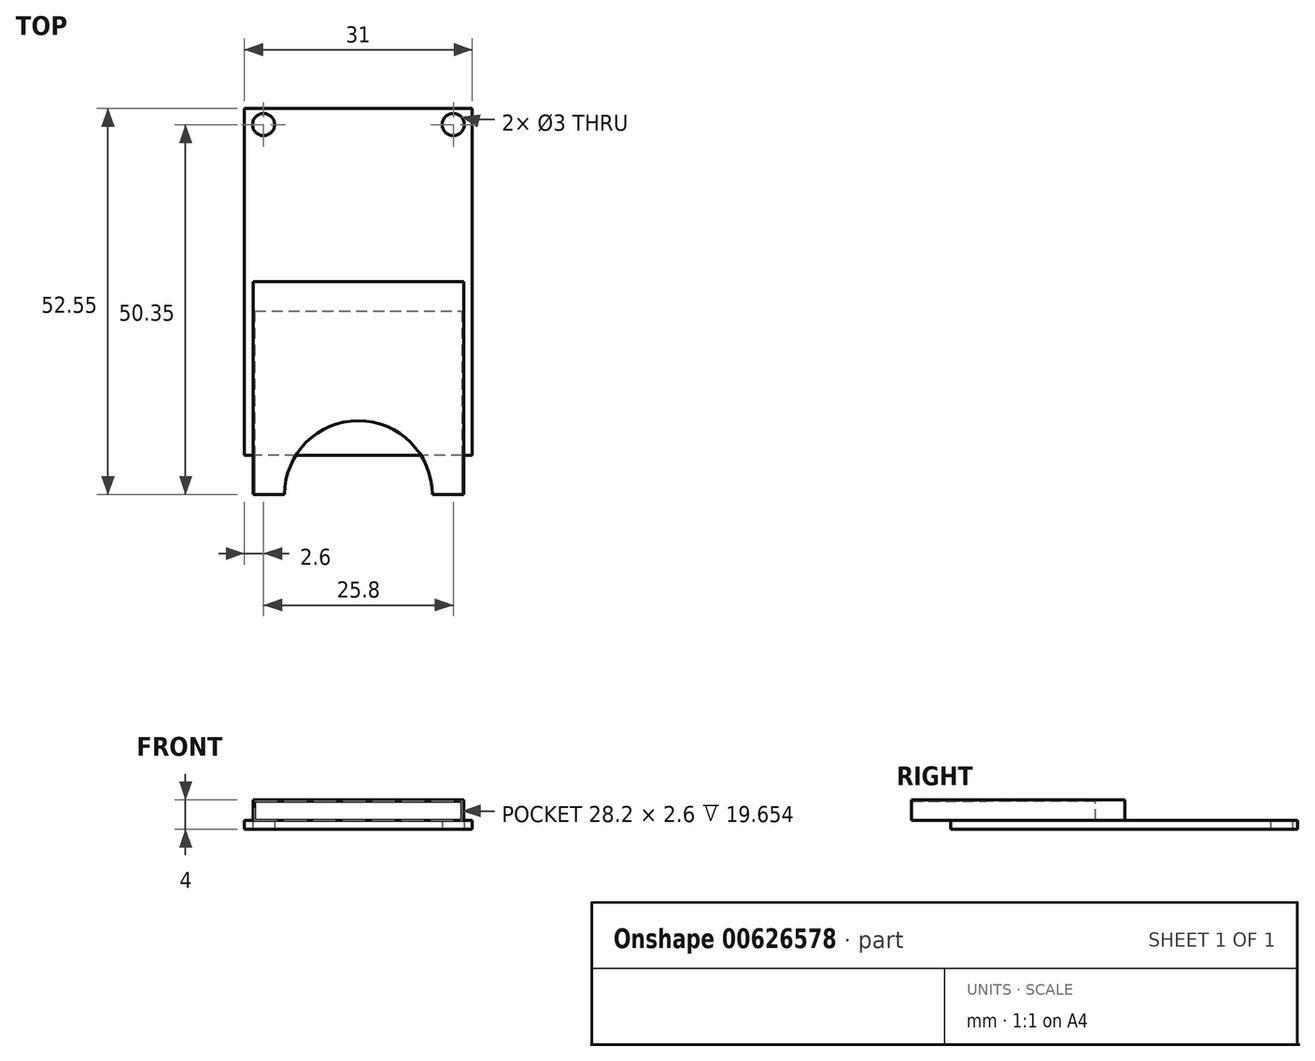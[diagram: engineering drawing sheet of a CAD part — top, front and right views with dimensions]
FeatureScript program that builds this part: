
annotation { "Feature Type Name" : "Feature", "Feature Type Description" : "" }
export const myFeature = defineFeature(function(context is Context, id is Id, definition is map)
    precondition{}
    {
        {
            var Q0;
            Q0=qCreatedBy(makeId("Top.planeOp"),FACE);
            var sketch = newSketch(context, id + "F0", { "sketchPlane" : qUnion([Q0])});
            skLineSegment(sketch, "E0.bottom", {"start": v(15.5, 23.6) * mm, "end": v(-15.5, 23.6) * mm});
            skLineSegment(sketch, "E0.top", {"start": v(15.5, -23.6) * mm, "end": v(-15.5, -23.6) * mm});
            skLineSegment(sketch, "E0.left", {"start": v(15.5, 23.6) * mm, "end": v(15.5, -23.6) * mm});
            skLineSegment(sketch, "E0.right", {"start": v(-15.5, 23.6) * mm, "end": v(-15.5, -23.6) * mm});
            skPoint(sketch, "E0.middle", {"position": v(0, 0) * mm});
            skCircle(sketch, "E1", {"center": v(-12.9, 21.4) * mm, "radius": 1.5 * mm});
            skCircle(sketch, "E2", {"center": v(12.9, 21.4) * mm, "radius": 1.5 * mm});
            skLineSegment(sketch, "E3", {"start": v(0, 23.6) * mm, "end": v(0, -23.6) * mm, "construction": true});
            skSolve(sketch);
        }
        {
            var Q0;
            Q0=makeQuery(id+"F0.imprint","IMPRINT",FACE,{"disambiguationData":[TD([[makeQuery(id+"F0.imprint","IMPRINT",EDGE,{"derivedFrom":sQuery(id+"F0.wireOp",EDGE,"E0.bottom")}),1.0]])]});
            extrude(context, id + "F1", {"entities" : qUnion([Q0]), "depth" : 1.2 * mm});
        }
        {
            var Q0;
            Q0=makeQuery(id+"F1.opExtrude","CAP_FACE",FACE,{"disambiguationData":[OSD([sQuery(id+"F0.wireOp",EDGE,"E0.bottom"),sQuery(id+"F0.wireOp",EDGE,"E0.top"),sQuery(id+"F0.wireOp",EDGE,"E0.left"),sQuery(id+"F0.wireOp",EDGE,"E0.right"),sQuery(id+"F0.wireOp",EDGE,"E1"),sQuery(id+"F0.wireOp",EDGE,"E2")])],"isStart":false});
            var sketch = newSketch(context, id + "F2", { "sketchPlane" : qUnion([Q0])});
            skLineSegment(sketch, "E4.bottom", {"start": v(14.3, -28.95) * mm, "end": v(-14.3, -28.95) * mm});
            skLineSegment(sketch, "E4.top", {"start": v(14.3, 0.05) * mm, "end": v(-14.3, 0.05) * mm});
            skLineSegment(sketch, "E4.left", {"start": v(14.3, -28.95) * mm, "end": v(14.3, 0.05) * mm});
            skLineSegment(sketch, "E4.right", {"start": v(-14.3, -28.95) * mm, "end": v(-14.3, 0.05) * mm});
            skPoint(sketch, "E4.middle", {"position": v(0, -14.45) * mm});
            skSolve(sketch);
        }
        {
            var Q0;
            Q0=qSketchRegion(id+"F2",true);
            extrude(context, id + "F3", {"entities" : qUnion([Q0]), "operationType" : NewBodyOperationType.ADD, "depth" : 2.8 * mm});
        }
        {
            var Q0;
            Q0=makeQuery(id+"F3.opExtrude","SWEPT_FACE",FACE,{"disambiguationData":[OSD([sQuery(id+"F2.wireOp",EDGE,"E4.bottom")])]});
            var sketch = newSketch(context, id + "F4", { "sketchPlane" : qUnion([Q0])});
            skLineSegment(sketch, "E5.bottom", {"start": v(-14.1, 1.2) * mm, "end": v(14.1, 1.2) * mm});
            skLineSegment(sketch, "E5.top", {"start": v(-14.1, 3.8) * mm, "end": v(14.1, 3.8) * mm});
            skLineSegment(sketch, "E5.left", {"start": v(-14.1, 1.2) * mm, "end": v(-14.1, 3.8) * mm});
            skLineSegment(sketch, "E5.right", {"start": v(14.1, 1.2) * mm, "end": v(14.1, 3.8) * mm});
            skSolve(sketch);
        }
        {
            var Q0;
            Q0=makeQuery(id+"F4.imprint","IMPRINT",FACE,{"disambiguationData":[TD([[makeQuery(id+"F4.imprint","IMPRINT",EDGE,{"derivedFrom":sQuery(id+"F4.wireOp",EDGE,"E5.bottom")}),-1.0]])]});
            extrude(context, id + "F5", {"entities" : qUnion([Q0]), "operationType" : NewBodyOperationType.REMOVE, "oppositeDirection" : true, "depth" : 25 * mm});
        }
        {
            var Q0;
            Q0=makeQuery(id+"F3.opExtrude","CAP_FACE",FACE,{"disambiguationData":[OSD([sQuery(id+"F2.wireOp",EDGE,"E4.bottom"),sQuery(id+"F2.wireOp",EDGE,"E4.top"),sQuery(id+"F2.wireOp",EDGE,"E4.left"),sQuery(id+"F2.wireOp",EDGE,"E4.right")])],"isStart":false});
            var sketch = newSketch(context, id + "F6", { "sketchPlane" : qUnion([Q0])});
            skArc(sketch, "E6", {"start": v(10.05, -28.95) * mm, "mid": v(0, -18.9) * mm, "end": v(-10.05, -28.95) * mm});
            skLineSegment(sketch, "E7", {"start": v(0, 0) * mm, "end": v(0, -28.95) * mm, "construction": true});
            skSolve(sketch);
        }
        {
            var Q0;
            {var subQ0=sQuery(id+"F6.wireOp",EDGE,"E6");Q0=makeQuery(id+"F6.imprint","IMPRINT",FACE,{"disambiguationData":[TD([[makeQuery(id+"F6.imprint","IMPRINT",EDGE,{"derivedFrom":subQ0}),1.0]])]});}
            extrude(context, id + "F7", {"entities" : qUnion([Q0]), "operationType" : NewBodyOperationType.REMOVE, "endBound" : BoundingType.UP_TO_NEXT, "oppositeDirection" : true, "depth" : 25 * mm});
        }
    });
